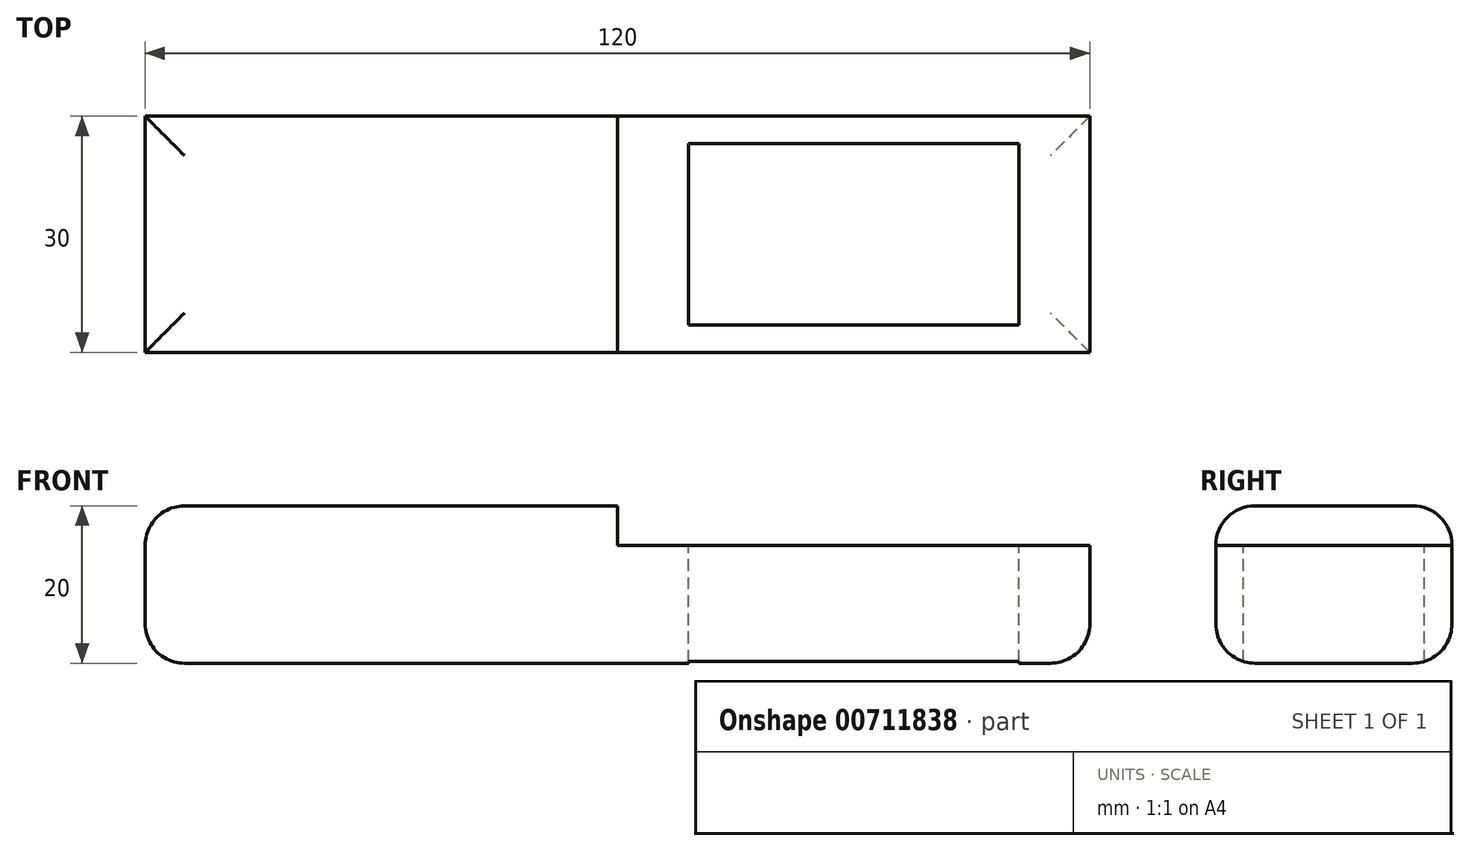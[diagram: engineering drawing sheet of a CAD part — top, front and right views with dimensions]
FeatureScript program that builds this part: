
annotation { "Feature Type Name" : "Feature", "Feature Type Description" : "" }
export const myFeature = defineFeature(function(context is Context, id is Id, definition is map)
    precondition{}
    {
        {
            var Q0;
            Q0=qCreatedBy(makeId("Top.planeOp"),FACE);
            var sketch = newSketch(context, id + "F0", { "sketchPlane" : qUnion([Q0])});
            skLineSegment(sketch, "E0.bottom", {"start": v(60, 15) * mm, "end": v(-60, 15) * mm});
            skLineSegment(sketch, "E0.top", {"start": v(60, -15) * mm, "end": v(-60, -15) * mm});
            skLineSegment(sketch, "E0.left", {"start": v(60, 15) * mm, "end": v(60, -15) * mm});
            skLineSegment(sketch, "E0.right", {"start": v(-60, 15) * mm, "end": v(-60, -15) * mm});
            skPoint(sketch, "E0.middle", {"position": v(0, 0) * mm});
            skSolve(sketch);
        }
        {
            var Q0;
            Q0=makeQuery(id+"F0.imprint","IMPRINT",FACE,{"disambiguationData":[TD([[makeQuery(id+"F0.imprint","IMPRINT",EDGE,{"derivedFrom":sQuery(id+"F0.wireOp",EDGE,"E0.bottom")}),1.0]])]});
            extrude(context, id + "F1", {"entities" : qUnion([Q0]), "depth" : 20 * mm, "offsetDistance" : 25 * mm});
        }
        {
            var Q0;
            Q0=makeQuery(id+"F1.opExtrude","CAP_FACE",FACE,{"disambiguationData":[OSD([sQuery(id+"F0.wireOp",EDGE,"E0.bottom"),sQuery(id+"F0.wireOp",EDGE,"E0.top"),sQuery(id+"F0.wireOp",EDGE,"E0.left"),sQuery(id+"F0.wireOp",EDGE,"E0.right")])],"isStart":false});
            var sketch = newSketch(context, id + "F2", { "sketchPlane" : qUnion([Q0])});
            skLineSegment(sketch, "E1", {"start": v(-60, 0) * mm, "end": v(60, 0) * mm});
            skLineSegment(sketch, "E2", {"start": v(0, -15) * mm, "end": v(0, 0) * mm});
            skLineSegment(sketch, "E3", {"start": v(0, 0) * mm, "end": v(0, 15) * mm});
            skLineSegment(sketch, "E4", {"start": v(0, 0) * mm, "end": v(30, 0) * mm});
            skLineSegment(sketch, "E5", {"start": v(30, 0) * mm, "end": v(60, 0) * mm});
            skLineSegment(sketch, "E6.bottom", {"start": v(51, 11.5) * mm, "end": v(9, 11.5) * mm});
            skLineSegment(sketch, "E6.top", {"start": v(51, -11.5) * mm, "end": v(9, -11.5) * mm});
            skLineSegment(sketch, "E6.left", {"start": v(51, 11.5) * mm, "end": v(51, -11.5) * mm});
            skLineSegment(sketch, "E6.right", {"start": v(9, 11.5) * mm, "end": v(9, -11.5) * mm});
            skPoint(sketch, "E6.middle", {"position": v(30, 0) * mm});
            skSolve(sketch);
        }
        {
            var Q0;
            {var subQ0=sQuery(id+"F2.wireOp",EDGE,"E6.bottom");Q0=makeQuery(id+"F2.imprint","IMPRINT",FACE,{"disambiguationData":[TD([[makeQuery(id+"F2.imprint","IMPRINT",EDGE,{"derivedFrom":subQ0}),1.0]])]});}
            var Q1;
            {var subQ0=sQuery(id+"F2.wireOp",EDGE,"E6.top");Q1=makeQuery(id+"F2.imprint","IMPRINT",FACE,{"disambiguationData":[TD([[makeQuery(id+"F2.imprint","IMPRINT",EDGE,{"derivedFrom":subQ0}),-1.0]])]});}
            extrude(context, id + "F3", {"entities" : qUnion([Q0, Q1]), "operationType" : NewBodyOperationType.REMOVE, "oppositeDirection" : true, "depth" : 25 * mm, "offsetDistance" : 25 * mm});
        }
        {
            var Q0;
            {var subQ8=sQuery(id+"F2.wireOp",EDGE,"E3");Q0=makeQuery(id+"F2.imprint","IMPRINT",FACE,{"disambiguationData":[TD([[makeQuery(id+"F2.imprint","IMPRINT",EDGE,{"derivedFrom":subQ8}),-1.0]])]});}
            var Q1;
            {var subQ2=sQuery(id+"F2.wireOp",EDGE,"E2");Q1=makeQuery(id+"F2.imprint","IMPRINT",FACE,{"disambiguationData":[TD([[makeQuery(id+"F2.imprint","IMPRINT",EDGE,{"derivedFrom":subQ2}),-1.0]])]});}
            extrude(context, id + "F4", {"entities" : qUnion([Q0, Q1]), "operationType" : NewBodyOperationType.REMOVE, "oppositeDirection" : true, "depth" : 5 * mm, "offsetDistance" : 25 * mm});
        }
        {
            var Q0;
            Q0=makeQuery(id+"F1.opExtrude","CAP_EDGE",EDGE,{"disambiguationData":[OSD([sQuery(id+"F0.wireOp",EDGE,"E0.top")])],"isStart":false});
            var Q1;
            Q1=makeQuery(id+"F1.opExtrude","CAP_EDGE",EDGE,{"disambiguationData":[OSD([sQuery(id+"F0.wireOp",EDGE,"E0.bottom")])],"isStart":false});
            var Q2;
            Q2=makeQuery(id+"F1.opExtrude","CAP_EDGE",EDGE,{"disambiguationData":[OSD([sQuery(id+"F0.wireOp",EDGE,"E0.top")])],"isStart":true});
            var Q3;
            Q3=makeQuery(id+"F1.opExtrude","CAP_EDGE",EDGE,{"disambiguationData":[OSD([sQuery(id+"F0.wireOp",EDGE,"E0.bottom")])],"isStart":true});
            var Q4;
            Q4=makeQuery(id+"F1.opExtrude","CAP_EDGE",EDGE,{"disambiguationData":[OSD([sQuery(id+"F0.wireOp",EDGE,"E0.left")])],"isStart":true});
            var Q5;
            Q5=makeQuery(id+"F1.opExtrude","CAP_EDGE",EDGE,{"disambiguationData":[OSD([sQuery(id+"F0.wireOp",EDGE,"E0.right")])],"isStart":true});
            var Q6;
            Q6=makeQuery(id+"F1.opExtrude","CAP_EDGE",EDGE,{"disambiguationData":[OSD([sQuery(id+"F0.wireOp",EDGE,"E0.right")])],"isStart":false});
            fillet(context, id + "F5", {"entities" : qUnion([Q0, Q1, Q2, Q3, Q4, Q5, Q6]), "radius" : 5 * mm, "tangentPropagation" : true, "allowEdgeOverflow" : false});
        }
    });
